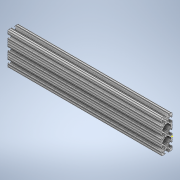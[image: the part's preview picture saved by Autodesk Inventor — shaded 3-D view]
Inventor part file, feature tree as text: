
AUTODESK INVENTOR PART (.ipt)
format: ipt  version: 2020 (Build 240168000, 168)  size: 384,000 bytes
history: native  units: in
note: dims shown in document units (in); Inventor stores cm internally (conversion verified against a paired STEP export)
features: sketch x2, extrude x1
ambient origin geometry x8: Origin, YZ Plane, XZ Plane, XY Plane, X Axis, Y Axis, Z Axis, Center Point
bodies: Solid1 (feature_tree)
feature tree (3):
  extrude  "Extrusion1"  [1 undecoded]
  sketch  "Sketch2"
  sketch  "Sketch1"  dims[d0=14.0in d1=0.0in]
note: 1 required parameter value undecoded (feature->parameter linkage not recoverable at this tier; creation-order binding heuristic only, values carry confidence <= 0.55)
